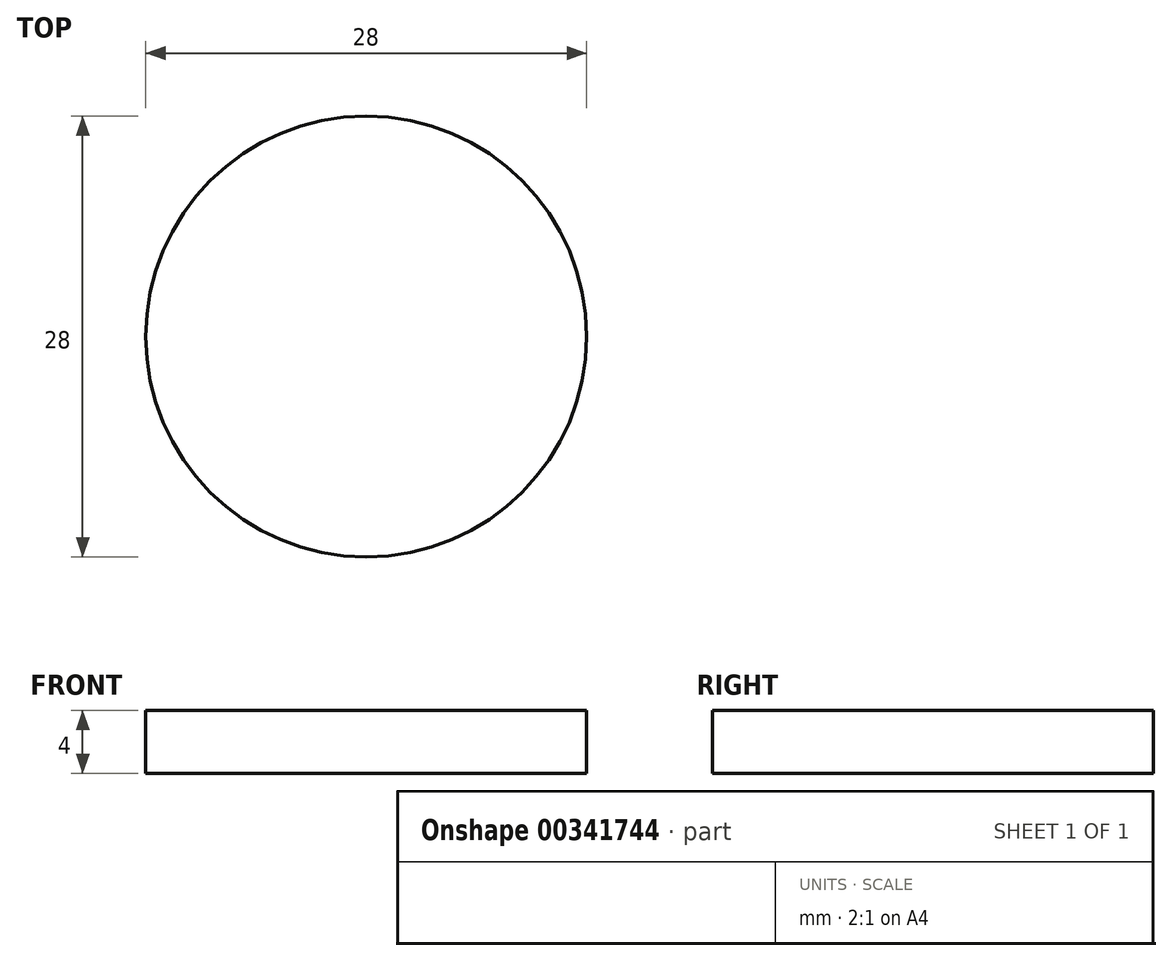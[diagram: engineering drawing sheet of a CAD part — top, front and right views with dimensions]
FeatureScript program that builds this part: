
annotation { "Feature Type Name" : "Feature", "Feature Type Description" : "" }
export const myFeature = defineFeature(function(context is Context, id is Id, definition is map)
    precondition{}
    {
        {
            var Q0;
            Q0=qCreatedBy(makeId("Top.planeOp"),FACE);
            var sketch = newSketch(context, id + "F0", { "sketchPlane" : qUnion([Q0])});
            skCircle(sketch, "E0", {"center": v(0, 0) * mm, "radius": 14 * mm});
            skSolve(sketch);
        }
        {
            var Q0;
            Q0=makeQuery(id+"F0.imprint","IMPRINT",FACE,{"disambiguationData":[TD([[makeQuery(id+"F0.imprint","IMPRINT",EDGE,{"derivedFrom":sQuery(id+"F0.wireOp",EDGE,"E0")}),1.0]])]});
            extrude(context, id + "F1", {"entities" : qUnion([Q0]), "depth" : 4 * mm});
        }
    });
